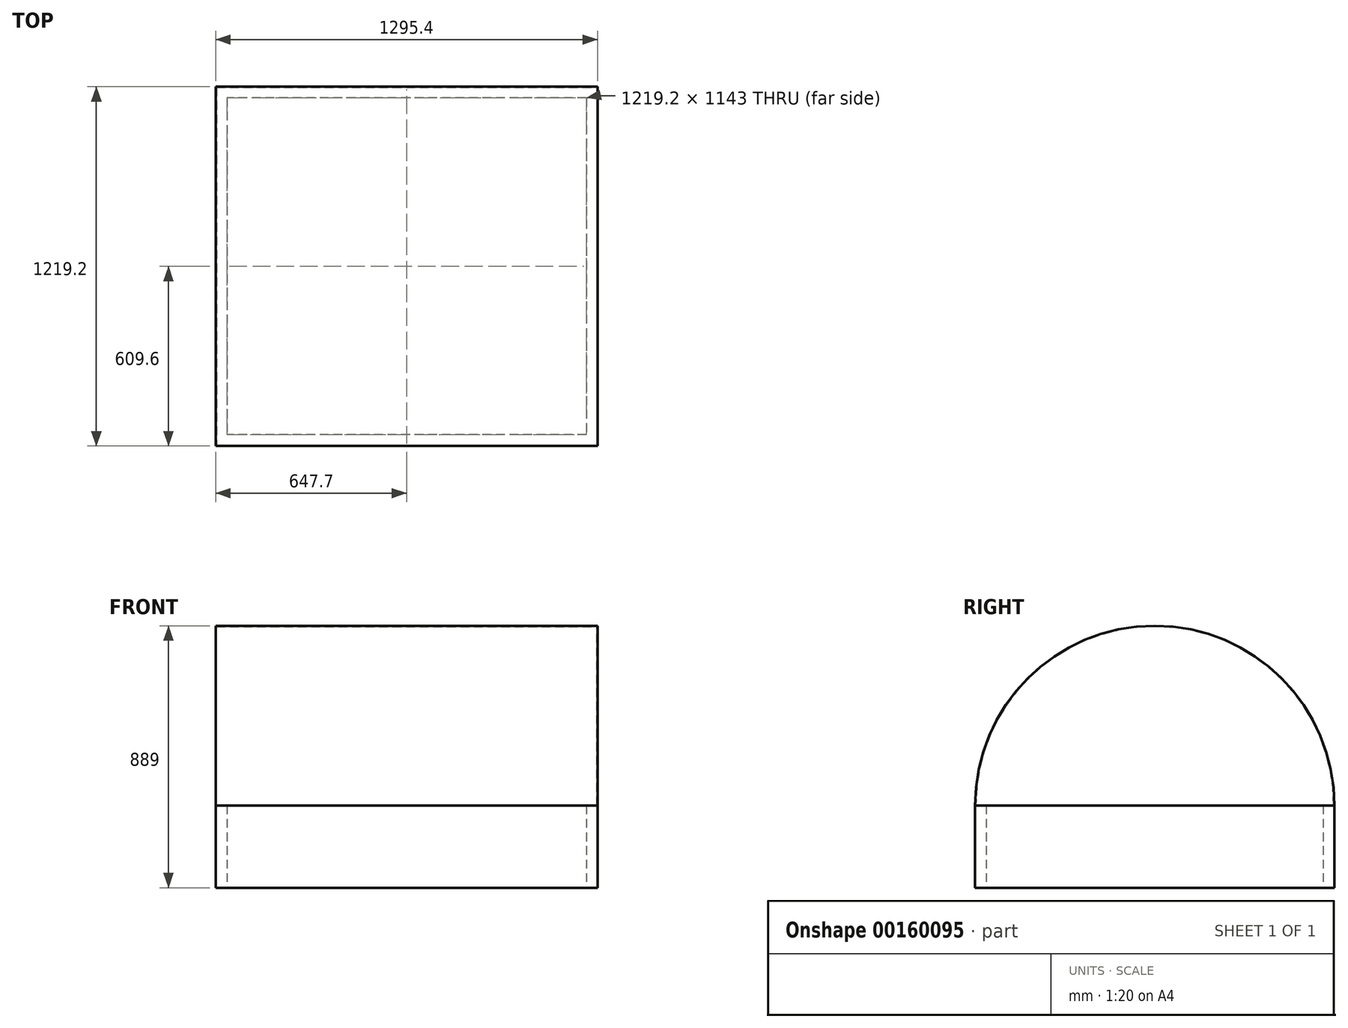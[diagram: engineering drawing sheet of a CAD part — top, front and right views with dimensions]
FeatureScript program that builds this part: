
annotation { "Feature Type Name" : "Feature", "Feature Type Description" : "" }
export const myFeature = defineFeature(function(context is Context, id is Id, definition is map)
    precondition{}
    {
        {
            var Q0;
            Q0=qCreatedBy(makeId("Top.planeOp"),FACE);
            var sketch = newSketch(context, id + "F0", { "sketchPlane" : qUnion([Q0])});
            skLineSegment(sketch, "E0.bottom", {"start": v(647.7, 609.6) * mm, "end": v(-647.7, 609.6) * mm});
            skLineSegment(sketch, "E0.top", {"start": v(647.7, -609.6) * mm, "end": v(-647.7, -609.6) * mm});
            skLineSegment(sketch, "E0.left", {"start": v(647.7, 609.6) * mm, "end": v(647.7, -609.6) * mm});
            skLineSegment(sketch, "E0.right", {"start": v(-647.7, 609.6) * mm, "end": v(-647.7, -609.6) * mm});
            skPoint(sketch, "E0.middle", {"position": v(0, 0) * mm});
            skLineSegment(sketch, "E1.0", {"start": v(-609.6, 571.5) * mm, "end": v(-609.6, -571.5) * mm});
            skLineSegment(sketch, "E1.1", {"start": v(609.6, 571.5) * mm, "end": v(-609.6, 571.5) * mm});
            skLineSegment(sketch, "E1.2", {"start": v(609.6, 571.5) * mm, "end": v(609.6, -571.5) * mm});
            skLineSegment(sketch, "E1.3", {"start": v(609.6, -571.5) * mm, "end": v(-609.6, -571.5) * mm});
            skSolve(sketch);
        }
        {
            var Q0;
            Q0 = qSketchRegion(id + "F0", true);
            extrude(context, id + "F1", {"entities" : qUnion([Q0]), "depth" : 279.4 * mm});
        }
        {
            var Q0;
            Q0=makeQuery(id+"F1.opExtrude","SWEPT_FACE",FACE,{"disambiguationData":[OSD([sQuery(id+"F0.wireOp",EDGE,"E0.left")])]});
            var sketch = newSketch(context, id + "F2", { "sketchPlane" : qUnion([Q0])});
            skArc(sketch, "E2", {"start": v(609.6, 279.4) * mm, "mid": v(0, 889) * mm, "end": v(-609.6, 279.4) * mm});
            skLineSegment(sketch, "E3.0", {"start": v(609.6, 279.4) * mm, "end": v(-609.6, 279.4) * mm});
            skSolve(sketch);
        }
        {
            var Q0;
            Q0 = qSketchRegion(id + "F2", true);
            var Q1;
            Q1=makeQuery(id+"F1.opExtrude","SWEPT_FACE",FACE,{"disambiguationData":[OSD([sQuery(id+"F0.wireOp",EDGE,"E0.right")])]});
            extrude(context, id + "F3", {"entities" : qUnion([Q0]), "endBound" : BoundingType.UP_TO_SURFACE, "oppositeDirection" : true, "endBoundEntityFace" : qUnion([Q1]), "depth" : 25 * mm});
        }
        {
            var Q0;
            Q0=makeQuery(id+"F3.opExtrude","SWEPT_FACE",FACE,{"disambiguationData":[OSD([sQuery(id+"F2.wireOp",EDGE,"E3.0")])]});
            shell(context, id + "F4", {"entities" : qUnion([Q0]), "thickness" : 2.5 * mm});
        }
    });
